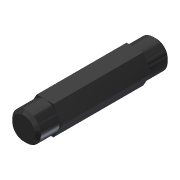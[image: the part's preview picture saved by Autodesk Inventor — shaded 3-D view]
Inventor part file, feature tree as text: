
AUTODESK INVENTOR PART (.ipt)
format: ipt  version: 2013 (Build 170138000, 138)  size: 86,528 bytes
history: native  units: in
note: dims shown in document units (in); Inventor stores cm internally (conversion verified against a paired STEP export)
features: chamfer x1, other x1, imported_body x1
ambient origin geometry x8: Origin, YZ Plane, XZ Plane, XY Plane, X Axis, Y Axis, Z Axis, Center Point
feature tree (3):
  chamfer  "Chamfer1"  [1 undecoded]
  other  "217-2428-004 Rev31"
  imported_body  "Base1"
note: 1 required parameter value undecoded (feature->parameter linkage not recoverable at this tier; creation-order binding heuristic only, values carry confidence <= 0.55)
